annotation { "Feature Type Name" : "Feature", "Feature Type Description" : "" }
export const myFeature = defineFeature(function(context is Context, id is Id, definition is map)
    precondition{}
    {
        {
            var Q0;
            Q0=qCreatedBy(makeId("Front.planeOp"),FACE);
            var sketch = newSketch(context, id + "F0", { "sketchPlane" : qUnion([Q0])});
            skLineSegment(sketch, "E0.bottom", {"start": v(-17.2, 17) * mm, "end": v(17.2, 17) * mm});
            skLineSegment(sketch, "E0.top", {"start": v(-17.2, -17) * mm, "end": v(17.2, -17) * mm});
            skLineSegment(sketch, "E0.left", {"start": v(-17.2, 17) * mm, "end": v(-17.2, -17) * mm});
            skLineSegment(sketch, "E0.right", {"start": v(17.2, 17) * mm, "end": v(17.2, -17) * mm});
            skPoint(sketch, "E0.middle", {"position": v(0, 0) * mm});
            skCircle(sketch, "E1", {"center": v(-20.7, 15.45) * mm, "radius": 1.5 * mm});
            skLineSegment(sketch, "E2.bottom", {"start": v(-21.08, 18) * mm, "end": v(-17.9, 18) * mm});
            skLineSegment(sketch, "E2.top", {"start": v(-21.18, 12.9) * mm, "end": v(-17.9, 12.9) * mm});
            skLineSegment(sketch, "E2.left", {"start": v(-23.5, 15.45) * mm, "end": v(-23.5, 15.45) * mm});
            skLineSegment(sketch, "E2.right", {"start": v(-17.9, 18) * mm, "end": v(-17.9, 12.9) * mm});
            skLineSegment(sketch, "E3.bottom", {"start": v(-17.9, 18) * mm, "end": v(-15.9, 18) * mm});
            skLineSegment(sketch, "E3.top", {"start": v(-17.9, -18) * mm, "end": v(-15.9, -18) * mm});
            skLineSegment(sketch, "E3.left", {"start": v(-17.9, 18) * mm, "end": v(-17.9, -18) * mm});
            skLineSegment(sketch, "E3.right", {"start": v(17.9, 18) * mm, "end": v(17.9, -18) * mm});
            skPoint(sketch, "E4", {"position": v(-15.9, 17) * mm});
            skLineSegment(sketch, "E5", {"start": v(-15.9, 17) * mm, "end": v(-15.9, 18) * mm});
            skLineSegment(sketch, "E6.MirrorCS", {"start": v(15.9, 17) * mm, "end": v(15.9, 18) * mm});
            skLineSegment(sketch, "E7.MirrorCS", {"start": v(21.18, 18) * mm, "end": v(17.9, 18) * mm});
            skPoint(sketch, "E8.MirrorP", {"position": v(15.9, 17) * mm});
            skCircle(sketch, "E9.MirrorC", {"center": v(20.7, 15.45) * mm, "radius": 1.5 * mm});
            skLineSegment(sketch, "E10.MirrorCS", {"start": v(21.18, 12.9) * mm, "end": v(17.9, 12.9) * mm});
            skPoint(sketch, "E11.MirrorP", {"position": v(-20.7, -15.45) * mm});
            skLineSegment(sketch, "E12.MirrorCS", {"start": v(-21.18, -12.9) * mm, "end": v(-17.9, -12.9) * mm});
            skLineSegment(sketch, "E13.MirrorCS", {"start": v(-21.18, -18) * mm, "end": v(-17.9, -18) * mm});
            skCircle(sketch, "E14.MirrorC", {"center": v(-20.7, -15.45) * mm, "radius": 1.5 * mm});
            skLineSegment(sketch, "E15.MirrorCS", {"start": v(-15.9, -17) * mm, "end": v(-15.9, -18) * mm});
            skPoint(sketch, "E16.MirrorP", {"position": v(20.7, -15.45) * mm});
            skCircle(sketch, "E17.MirrorC", {"center": v(20.7, -15.45) * mm, "radius": 1.5 * mm});
            skLineSegment(sketch, "E18.MirrorCS", {"start": v(21.18, -12.9) * mm, "end": v(17.9, -12.9) * mm});
            skLineSegment(sketch, "E19.MirrorCS", {"start": v(21.18, -18) * mm, "end": v(17.9, -18) * mm});
            skLineSegment(sketch, "E20.MirrorCS", {"start": v(15.9, -17) * mm, "end": v(15.9, -18) * mm});
            skLineSegment(sketch, "E21.trimOffspring", {"start": v(15.9, 18) * mm, "end": v(17.9, 18) * mm});
            skLineSegment(sketch, "E22.trimOffspring", {"start": v(15.9, -18) * mm, "end": v(17.9, -18) * mm});
            skPoint(sketch, "E23", {"position": v(-20.7, 18) * mm});
            skPoint(sketch, "E24", {"position": v(-23.5, 15.45) * mm});
            skPoint(sketch, "E25", {"position": v(-20.7, 12.9) * mm});
            skArc(sketch, "E26", {"start": v(-20.8, 18) * mm, "mid": v(-23.5, 15.4) * mm, "end": v(-20.7, 12.9) * mm});
            skPoint(sketch, "E26.second.point", {"position": v(-20.8, 18) * mm});
            skPoint(sketch, "E27.orphan", {"position": v(-23.5, 18) * mm});
            skPoint(sketch, "E28.orphan", {"position": v(-23.5, 12.9) * mm});
            skLineSegment(sketch, "E29", {"start": v(20.7, 15.45) * mm, "end": v(20.94, 15.45) * mm});
            skPoint(sketch, "E30", {"position": v(23.5, 15.45) * mm});
            skArc(sketch, "E31", {"start": v(20.7, 12.9) * mm, "mid": v(23.5, 15.45) * mm, "end": v(20.7, 18) * mm});
            skArc(sketch, "E32", {"start": v(20.7, -18) * mm, "mid": v(23.5, -15.45) * mm, "end": v(20.7, -12.9) * mm});
            skArc(sketch, "E33", {"start": v(-20.7, -12.9) * mm, "mid": v(-23.5, -15.45) * mm, "end": v(-20.7, -18) * mm});
            skSolve(sketch);
        }
        {
            var Q0;
            Q0=makeQuery(id+"F0.imprint","IMPRINT",FACE,{"disambiguationData":[TD([[makeQuery(id+"F0.imprint","IMPRINT",EDGE,{"derivedFrom":sQuery(id+"F0.wireOp",EDGE,"E17.MirrorC")}),-1.0]])]});
            var Q1;
            {var subQ0=sQuery(id+"F0.wireOp",EDGE,"E0.left");Q1=makeQuery(id+"F0.imprint","IMPRINT",FACE,{"disambiguationData":[TD([[makeQuery(id+"F0.imprint","IMPRINT",EDGE,{"derivedFrom":subQ0}),1.0]])]});}
            var Q2;
            {var subQ2=sQuery(id+"F0.wireOp",EDGE,"E0.right");Q2=makeQuery(id+"F0.imprint","IMPRINT",FACE,{"disambiguationData":[TD([[makeQuery(id+"F0.imprint","IMPRINT",EDGE,{"derivedFrom":subQ2}),1.0]])]});}
            var Q3;
            Q3=makeQuery(id+"F0.imprint","IMPRINT",FACE,{"disambiguationData":[TD([[makeQuery(id+"F0.imprint","IMPRINT",EDGE,{"derivedFrom":sQuery(id+"F0.wireOp",EDGE,"E9.MirrorC")}),1.0]])]});
            var Q4;
            Q4=makeQuery(id+"F0.imprint","IMPRINT",FACE,{"disambiguationData":[TD([[makeQuery(id+"F0.imprint","IMPRINT",EDGE,{"derivedFrom":sQuery(id+"F0.wireOp",EDGE,"E1")}),-1.0]])]});
            var Q5;
            {var subQ0=sQuery(id+"F0.wireOp",EDGE,"E0.left");Q5=makeQuery(id+"F0.imprint","IMPRINT",FACE,{"disambiguationData":[TD([[makeQuery(id+"F0.imprint","IMPRINT",EDGE,{"derivedFrom":subQ0}),-1.0]])]});}
            var Q6;
            Q6=makeQuery(id+"F0.imprint","IMPRINT",FACE,{"disambiguationData":[TD([[makeQuery(id+"F0.imprint","IMPRINT",EDGE,{"derivedFrom":sQuery(id+"F0.wireOp",EDGE,"E14.MirrorC")}),1.0]])]});
            extrude(context, id + "F1", {"entities" : qUnion([Q0, Q1, Q2, Q3, Q4, Q5, Q6]), "depth" : 1.6 * mm});
        }
        {
            var Q0;
            {var subQ0=sQuery(id+"F0.wireOp",EDGE,"E0.left");Q0=makeQuery(id+"F0.imprint","IMPRINT",FACE,{"disambiguationData":[TD([[makeQuery(id+"F0.imprint","IMPRINT",EDGE,{"derivedFrom":subQ0}),1.0]])]});}
            extrude(context, id + "F2", {"entities" : qUnion([Q0]), "operationType" : NewBodyOperationType.ADD, "depth" : 3.1 * mm});
        }
        {
            var Q0;
            Q0=makeQuery(id+"F1.opExtrude","CAP_FACE",FACE,{"disambiguationData":[OSD([sQuery(id+"F0.wireOp",EDGE,"E0.bottom"),sQuery(id+"F0.wireOp",EDGE,"E0.top"),sQuery(id+"F0.wireOp",EDGE,"E1"),sQuery(id+"F0.wireOp",EDGE,"E2.bottom"),sQuery(id+"F0.wireOp",EDGE,"E2.top"),sQuery(id+"F0.wireOp",EDGE,"E3.bottom"),sQuery(id+"F0.wireOp",EDGE,"E3.top"),sQuery(id+"F0.wireOp",EDGE,"E3.left"),sQuery(id+"F0.wireOp",EDGE,"E5"),sQuery(id+"F0.wireOp",EDGE,"E6.MirrorCS"),sQuery(id+"F0.wireOp",EDGE,"E7.MirrorCS"),sQuery(id+"F0.wireOp",EDGE,"E9.MirrorC"),sQuery(id+"F0.wireOp",EDGE,"E10.MirrorCS"),sQuery(id+"F0.wireOp",EDGE,"E3.right"),sQuery(id+"F0.wireOp",EDGE,"E12.MirrorCS"),sQuery(id+"F0.wireOp",EDGE,"E13.MirrorCS"),sQuery(id+"F0.wireOp",EDGE,"E14.MirrorC"),sQuery(id+"F0.wireOp",EDGE,"E15.MirrorCS"),sQuery(id+"F0.wireOp",EDGE,"E17.MirrorC"),sQuery(id+"F0.wireOp",EDGE,"E18.MirrorCS"),sQuery(id+"F0.wireOp",EDGE,"E19.MirrorCS"),sQuery(id+"F0.wireOp",EDGE,"E20.MirrorCS"),sQuery(id+"F0.wireOp",EDGE,"E21.trimOffspring"),sQuery(id+"F0.wireOp",EDGE,"E22.trimOffspring"),sQuery(id+"F0.wireOp",EDGE,"E26"),sQuery(id+"F0.wireOp",EDGE,"E31"),sQuery(id+"F0.wireOp",EDGE,"E32"),sQuery(id+"F0.wireOp",EDGE,"E33")])],"isStart":true});
            var sketch = newSketch(context, id + "F3", { "sketchPlane" : qUnion([Q0])});
            skCircle(sketch, "E34", {"center": v(14.34, -14.04) * mm, "radius": 0.25 * mm});
            skCircle(sketch, "E35.1.0.0", {"center": v(11.84, -14.04) * mm, "radius": 0.25 * mm});
            skCircle(sketch, "E35.2.0.0", {"center": v(9.34, -14.04) * mm, "radius": 0.25 * mm});
            skCircle(sketch, "E35.3.0.0", {"center": v(6.84, -14.03) * mm, "radius": 0.25 * mm});
            skCircle(sketch, "E35.4.0.0", {"center": v(4.34, -14.03) * mm, "radius": 0.25 * mm});
            skLineSegment(sketch, "E35.direction1", {"start": v(14.34, -14.04) * mm, "end": v(11.84, -14.04) * mm, "construction": true});
            skCircle(sketch, "E36.1.0.0", {"center": v(6.84, -15) * mm, "radius": 0.25 * mm});
            skCircle(sketch, "E36.1.0.1", {"center": v(14.34, -15) * mm, "radius": 0.25 * mm});
            skCircle(sketch, "E36.1.0.2", {"center": v(9.34, -15) * mm, "radius": 0.25 * mm});
            skCircle(sketch, "E36.1.0.3", {"center": v(4.34, -15) * mm, "radius": 0.25 * mm});
            skLineSegment(sketch, "E36.1.0.4", {"start": v(14.34, -15) * mm, "end": v(11.84, -15) * mm, "construction": true});
            skCircle(sketch, "E36.1.0.5", {"center": v(11.84, -15) * mm, "radius": 0.25 * mm});
            skLineSegment(sketch, "E36.direction1", {"start": v(4.34, -14.03) * mm, "end": v(4.34, -15) * mm, "construction": true});
            skLineSegment(sketch, "E37.bottom", {"start": v(3.35, -13.2) * mm, "end": v(15.3, -13.2) * mm});
            skLineSegment(sketch, "E37.top", {"start": v(3.35, -15.85) * mm, "end": v(15.3, -15.85) * mm});
            skLineSegment(sketch, "E37.left", {"start": v(3.35, -13.2) * mm, "end": v(3.35, -15.85) * mm});
            skLineSegment(sketch, "E37.right", {"start": v(15.3, -13.2) * mm, "end": v(15.3, -15.85) * mm});
            skSolve(sketch);
        }
        {
            var Q0;
            Q0=sQuery(id+"F3.wireOp",EDGE,"E36.1.0.0");
            var Q1;
            Q1=sQuery(id+"F3.wireOp",EDGE,"E36.1.0.1");
            var Q2;
            Q2=sQuery(id+"F3.wireOp",EDGE,"E35.4.0.0");
            var Q3;
            Q3=sQuery(id+"F3.wireOp",EDGE,"E35.3.0.0");
            var Q4;
            Q4=sQuery(id+"F3.wireOp",EDGE,"E35.2.0.0");
            var Q5;
            Q5=sQuery(id+"F3.wireOp",EDGE,"E34");
            var Q6;
            Q6=sQuery(id+"F3.wireOp",EDGE,"E36.1.0.2");
            var Q7;
            Q7=sQuery(id+"F3.wireOp",EDGE,"E36.1.0.3");
            var Q8;
            Q8=sQuery(id+"F3.wireOp",EDGE,"E36.1.0.5");
            var Q9;
            Q9=sQuery(id+"F3.wireOp",EDGE,"E35.1.0.0");
            extrude(context, id + "F4", {"bodyType" : ToolBodyType.SURFACE, "surfaceEntities" : qUnion([Q0, Q1, Q2, Q3, Q4, Q5, Q6, Q7, Q8, Q9]), "depth" : 6 * mm});
        }
        {
            var Q0;
            Q0=makeQuery(id+"F3.imprint","IMPRINT",FACE,{"disambiguationData":[TD([[makeQuery(id+"F3.imprint","IMPRINT",EDGE,{"derivedFrom":sQuery(id+"F3.wireOp",EDGE,"E34")}),-1.0]])]});
            extrude(context, id + "F5", {"entities" : qUnion([Q0]), "operationType" : NewBodyOperationType.ADD, "depth" : 2 * mm});
        }
        {
            var Q0;
            Q0=makeQuery(id+"F2.opExtrude","CAP_FACE",FACE,{"disambiguationData":[OSD([sQuery(id+"F0.wireOp",EDGE,"E0.bottom"),sQuery(id+"F0.wireOp",EDGE,"E0.top"),sQuery(id+"F0.wireOp",EDGE,"E0.left"),sQuery(id+"F0.wireOp",EDGE,"E0.right")])],"isStart":false});
            var sketch = newSketch(context, id + "F6", { "sketchPlane" : qUnion([Q0])});
            skText(sketch, "E38", { "text": "Touch Screen", "fontName": "RobotoSlab-Regular.ttf"});
            const initialGuessF6  = {"E38": [-0.00905, 0.00421, 1, 0, 0.002]};
            skSetInitialGuess(sketch, initialGuessF6);
            skSolve(sketch);
        }
        {
            var Q0;
            Q0=makeQuery(id+"F6.imprint","IMPRINT",FACE,{"disambiguationData":[TD([[makeQuery(id+"F6.imprint","IMPRINT",EDGE,{"derivedFrom":sQuery(id+"F6.wireOp",EDGE,"E38.sketch_text.stroke-83")}),-1.0]])]});
            var Q1;
            Q1=makeQuery(id+"F6.imprint","IMPRINT",FACE,{"disambiguationData":[TD([[makeQuery(id+"F6.imprint","IMPRINT",EDGE,{"derivedFrom":sQuery(id+"F6.wireOp",EDGE,"E38.sketch_text.stroke-60")}),-1.0]])]});
            var Q2;
            Q2=makeQuery(id+"F6.imprint","IMPRINT",FACE,{"disambiguationData":[TD([[makeQuery(id+"F6.imprint","IMPRINT",EDGE,{"derivedFrom":sQuery(id+"F6.wireOp",EDGE,"E38.sketch_text.stroke-36")}),-1.0]])]});
            var Q3;
            Q3=makeQuery(id+"F6.imprint","IMPRINT",FACE,{"disambiguationData":[TD([[makeQuery(id+"F6.imprint","IMPRINT",EDGE,{"derivedFrom":sQuery(id+"F6.wireOp",EDGE,"E38.sketch_text.stroke-16")}),-1.0]])]});
            var Q4;
            Q4=makeQuery(id+"F6.imprint","IMPRINT",FACE,{"disambiguationData":[TD([[makeQuery(id+"F6.imprint","IMPRINT",EDGE,{"derivedFrom":sQuery(id+"F6.wireOp",EDGE,"E38.sketch_text.stroke-0")}),-1.0]])]});
            var Q5;
            Q5=makeQuery(id+"F6.imprint","IMPRINT",FACE,{"disambiguationData":[TD([[makeQuery(id+"F6.imprint","IMPRINT",EDGE,{"derivedFrom":sQuery(id+"F6.wireOp",EDGE,"E38.sketch_text.stroke-109")}),-1.0]])]});
            var Q6;
            Q6=makeQuery(id+"F6.imprint","IMPRINT",FACE,{"disambiguationData":[TD([[makeQuery(id+"F6.imprint","IMPRINT",EDGE,{"derivedFrom":sQuery(id+"F6.wireOp",EDGE,"E38.sketch_text.stroke-139")}),-1.0]])]});
            var Q7;
            Q7=makeQuery(id+"F6.imprint","IMPRINT",FACE,{"disambiguationData":[TD([[makeQuery(id+"F6.imprint","IMPRINT",EDGE,{"derivedFrom":sQuery(id+"F6.wireOp",EDGE,"E38.sketch_text.stroke-162")}),-1.0]])]});
            var Q8;
            Q8=makeQuery(id+"F6.imprint","IMPRINT",FACE,{"disambiguationData":[TD([[makeQuery(id+"F6.imprint","IMPRINT",EDGE,{"derivedFrom":sQuery(id+"F6.wireOp",EDGE,"E38.sketch_text.stroke-181")}),-1.0]])]});
            var Q9;
            Q9=makeQuery(id+"F6.imprint","IMPRINT",FACE,{"disambiguationData":[TD([[makeQuery(id+"F6.imprint","IMPRINT",EDGE,{"derivedFrom":sQuery(id+"F6.wireOp",EDGE,"E38.sketch_text.stroke-205")}),-1.0]])]});
            var Q10;
            Q10=makeQuery(id+"F6.imprint","IMPRINT",FACE,{"disambiguationData":[TD([[makeQuery(id+"F6.imprint","IMPRINT",EDGE,{"derivedFrom":sQuery(id+"F6.wireOp",EDGE,"E38.sketch_text.stroke-229")}),-1.0]])]});
            extrude(context, id + "F7", {"entities" : qUnion([Q0, Q1, Q2, Q3, Q4, Q5, Q6, Q7, Q8, Q9, Q10]), "operationType" : NewBodyOperationType.ADD, "depth" : .25 * mm});
        }
    });